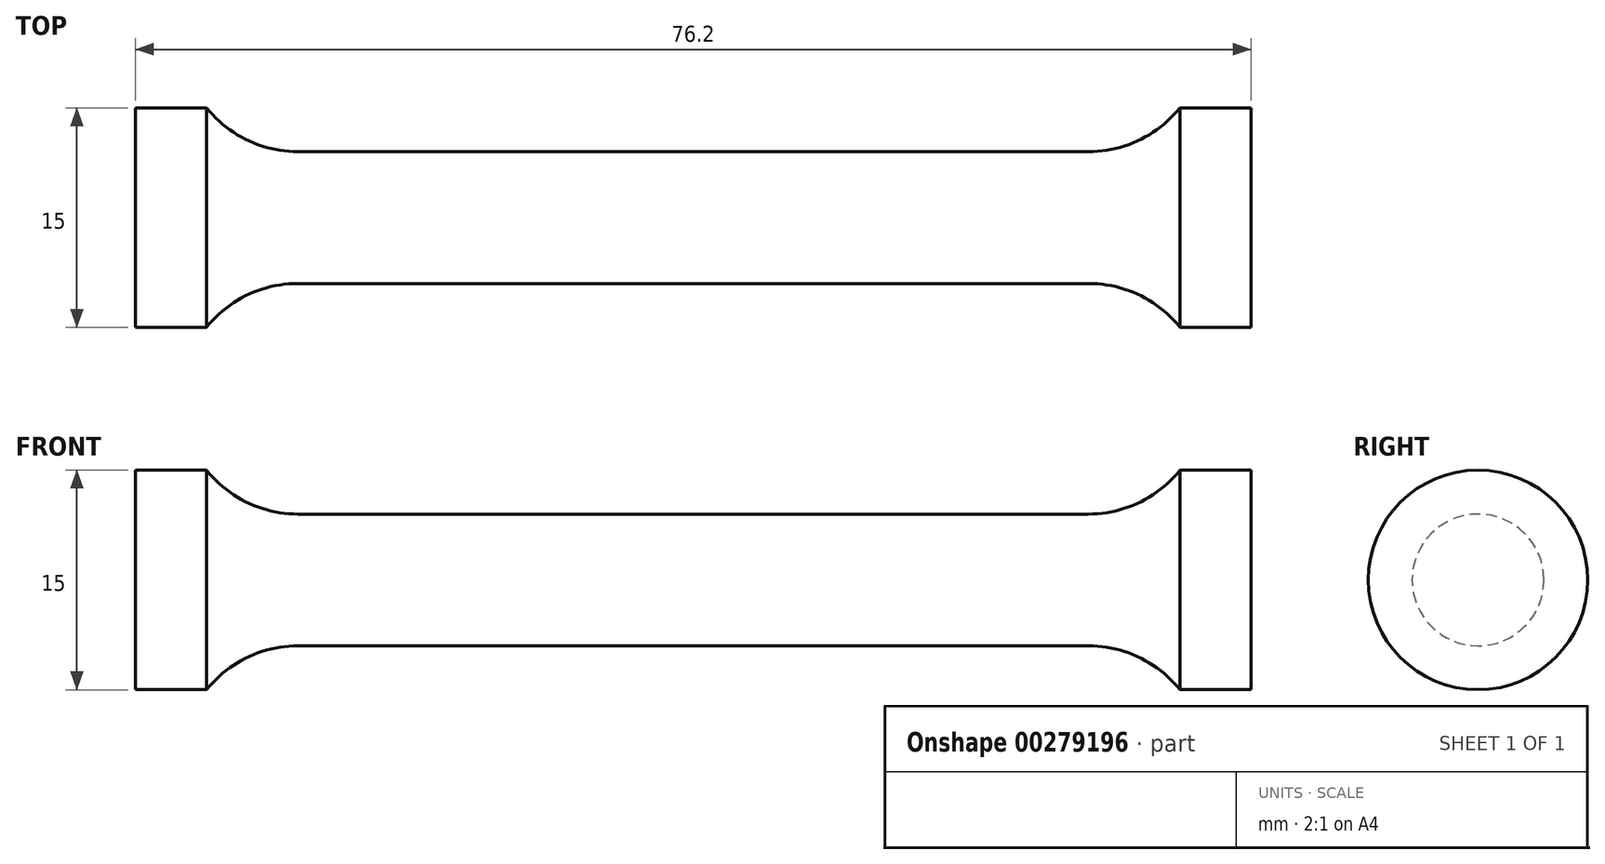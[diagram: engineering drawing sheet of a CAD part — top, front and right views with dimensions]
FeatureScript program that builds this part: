
annotation { "Feature Type Name" : "Feature", "Feature Type Description" : "" }
export const myFeature = defineFeature(function(context is Context, id is Id, definition is map)
    precondition{}
    {
        {
            var Q0;
            Q0=qCreatedBy(makeId("Front.planeOp"),FACE);
            var sketch = newSketch(context, id + "F0", { "sketchPlane" : qUnion([Q0])});
            skLineSegment(sketch, "E0", {"start": v(0, 4.5) * mm, "end": v(27, 4.5) * mm});
            skArc(sketch, "E1", {"start": v(27, 4.5) * mm, "mid": v(30.46, 5.29) * mm, "end": v(33.24, 7.5) * mm});
            skLineSegment(sketch, "E2", {"start": v(33.24, 7.5) * mm, "end": v(38.1, 7.5) * mm});
            skLineSegment(sketch, "E3", {"start": v(38.1, 7.5) * mm, "end": v(38.1, 0) * mm});
            skArc(sketch, "E4.MirrorCS", {"start": v(-27, 4.5) * mm, "mid": v(-30.46, 5.29) * mm, "end": v(-33.24, 7.5) * mm});
            skLineSegment(sketch, "E5.MirrorCS", {"start": v(-33.24, 7.5) * mm, "end": v(-38.1, 7.5) * mm});
            skLineSegment(sketch, "E6.MirrorCS", {"start": v(0, 4.5) * mm, "end": v(-27, 4.5) * mm});
            skLineSegment(sketch, "E7.MirrorCS", {"start": v(-38.1, 7.5) * mm, "end": v(-38.1, 0) * mm});
            skLineSegment(sketch, "E8", {"start": v(-38.1, 0) * mm, "end": v(38.1, 0) * mm});
            skSolve(sketch);
        }
        {
            var Q0;
            Q0=makeQuery(id+"F0.imprint","IMPRINT",FACE,{"disambiguationData":[TD([[makeQuery(id+"F0.imprint","IMPRINT",EDGE,{"derivedFrom":sQuery(id+"F0.wireOp",EDGE,"E0")}),-1.0]])]});
            var Q1;
            Q1=sQuery(id+"F0.wireOp",EDGE,"E8");
            revolve(context, id + "F1", {"entities" : qUnion([Q0]), "axis" : qUnion([Q1]), "revolveType" : RevolveType.FULL});
        }
    });
